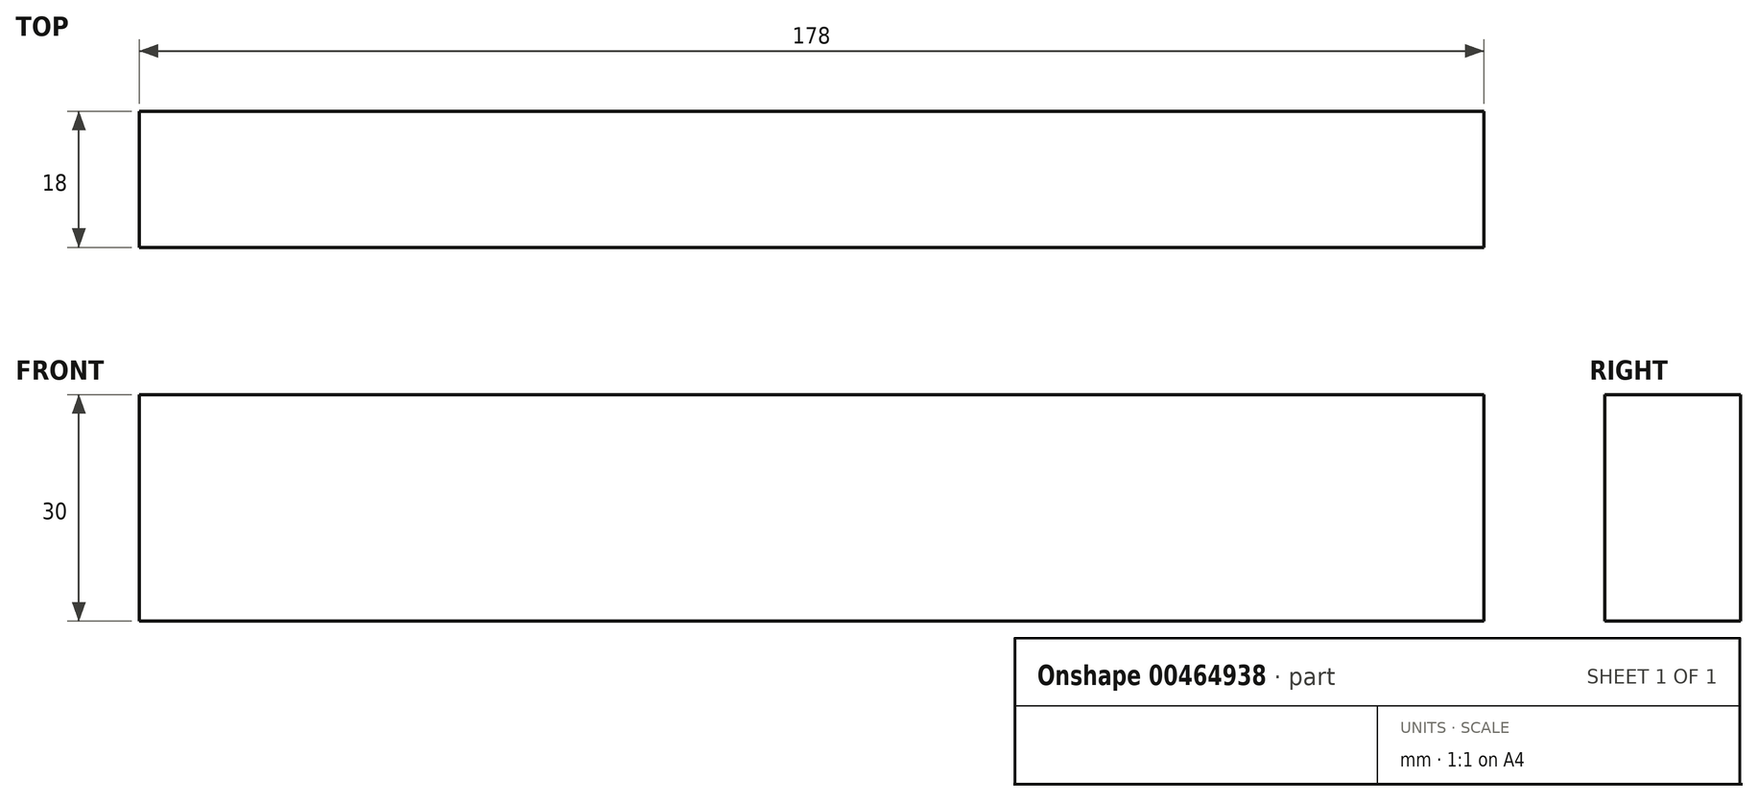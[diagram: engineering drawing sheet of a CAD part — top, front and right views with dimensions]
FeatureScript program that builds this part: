
annotation { "Feature Type Name" : "Feature", "Feature Type Description" : "" }
export const myFeature = defineFeature(function(context is Context, id is Id, definition is map)
    precondition{}
    {
        {
            var Q0;
            Q0=qCreatedBy(makeId("Right.planeOp"),FACE);
            var sketch = newSketch(context, id + "F0", { "sketchPlane" : qUnion([Q0])});
            skLineSegment(sketch, "E0.bottom", {"start": v(-9, 15) * mm, "end": v(9, 15) * mm});
            skLineSegment(sketch, "E0.top", {"start": v(-9, -15) * mm, "end": v(9, -15) * mm});
            skLineSegment(sketch, "E0.left", {"start": v(-9, 15) * mm, "end": v(-9, -15) * mm});
            skLineSegment(sketch, "E0.right", {"start": v(9, 15) * mm, "end": v(9, -15) * mm});
            skPoint(sketch, "E0.middle", {"position": v(0, 0) * mm});
            skSolve(sketch);
        }
        {
            var Q0;
            Q0=makeQuery(id+"F0.imprint","IMPRINT",FACE,{"disambiguationData":[TD([[makeQuery(id+"F0.imprint","IMPRINT",EDGE,{"derivedFrom":sQuery(id+"F0.wireOp",EDGE,"E0.bottom")}),-1.0]])]});
            extrude(context, id + "F1", {"entities" : qUnion([Q0]), "endBound" : BoundingType.SYMMETRIC, "depth" : (154 + 24) * mm, "offsetDistance" : 25 * mm});
        }
    });
